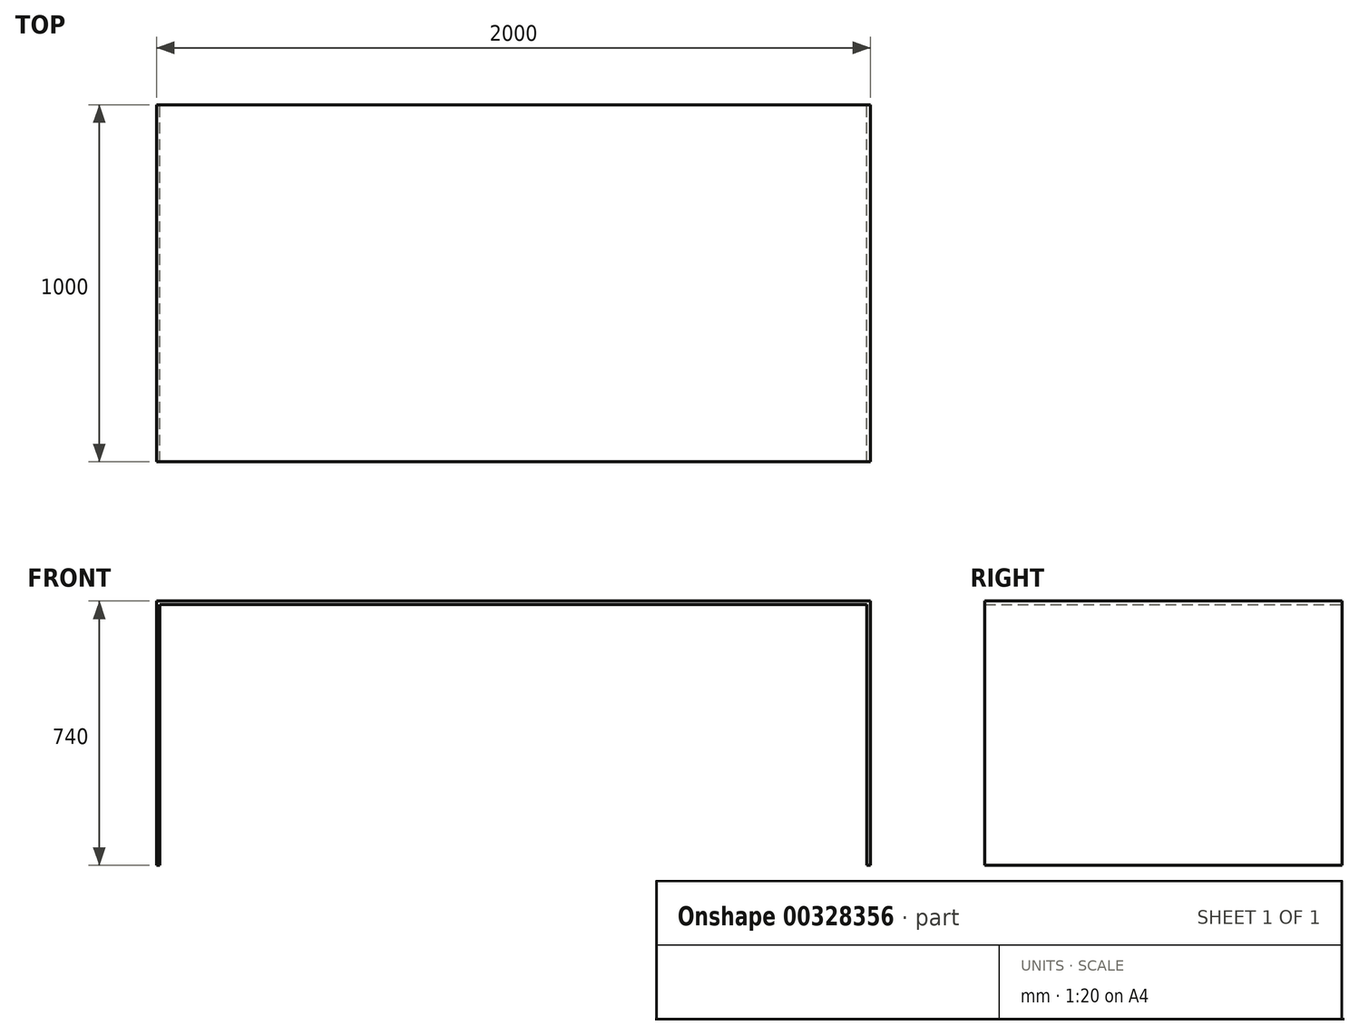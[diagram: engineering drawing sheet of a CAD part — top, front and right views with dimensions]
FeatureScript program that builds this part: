
annotation { "Feature Type Name" : "Feature", "Feature Type Description" : "" }
export const myFeature = defineFeature(function(context is Context, id is Id, definition is map)
    precondition{}
    {
        {
            var Q0;
            Q0=qCreatedBy(makeId("Front.planeOp"),FACE);
            var sketch = newSketch(context, id + "F0", { "sketchPlane" : qUnion([Q0])});
            skLineSegment(sketch, "E0", {"start": v(0, 0) * mm, "end": v(10, 0) * mm});
            skLineSegment(sketch, "E1", {"start": v(10, 0) * mm, "end": v(10, 730) * mm});
            skLineSegment(sketch, "E2", {"start": v(10, 730) * mm, "end": v(1990, 730) * mm});
            skLineSegment(sketch, "E3", {"start": v(1990, 730) * mm, "end": v(1990, 0) * mm});
            skLineSegment(sketch, "E4", {"start": v(1990, 0) * mm, "end": v(2000, 0) * mm});
            skLineSegment(sketch, "E5", {"start": v(2000, 0) * mm, "end": v(2000, 740) * mm});
            skLineSegment(sketch, "E6", {"start": v(2000, 740) * mm, "end": v(0, 740) * mm});
            skLineSegment(sketch, "E7", {"start": v(0, 740) * mm, "end": v(0, 0) * mm});
            skLineSegment(sketch, "E8", {"start": v(10, 730) * mm, "end": v(10, 740) * mm, "construction": true});
            skSolve(sketch);
        }
        {
            var Q0;
            Q0=makeQuery(id+"F0.imprint","IMPRINT",FACE,{"disambiguationData":[TD([[makeQuery(id+"F0.imprint","IMPRINT",EDGE,{"derivedFrom":sQuery(id+"F0.wireOp",EDGE,"E0")}),1.0]])]});
            extrude(context, id + "F1", {"entities" : qUnion([Q0]), "depth" : 1000 * mm});
        }
    });
